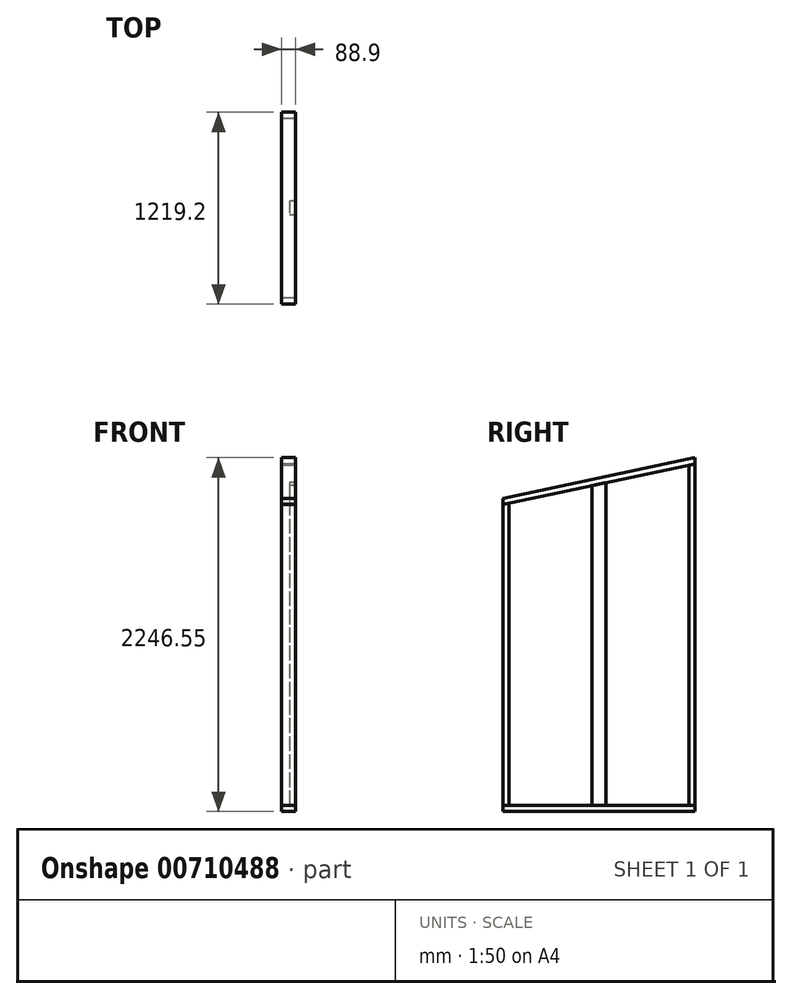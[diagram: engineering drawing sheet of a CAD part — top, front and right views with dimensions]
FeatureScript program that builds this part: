
annotation { "Feature Type Name" : "Feature", "Feature Type Description" : "" }
export const myFeature = defineFeature(function(context is Context, id is Id, definition is map)
    precondition{}
    {
        {
            var Q0;
            Q0=qCreatedBy(makeId("Right.planeOp"),FACE);
            var sketch = newSketch(context, id + "F0", { "sketchPlane" : qUnion([Q0])});
            skLineSegment(sketch, "E0", {"start": v(0, 0) * mm, "end": v(0, 1968.5) * mm});
            skLineSegment(sketch, "E1", {"start": v(0, 1968.5) * mm, "end": v(1397, 2265.44) * mm});
            skLineSegment(sketch, "E2", {"start": v(1397, 2265.44) * mm, "end": v(1397, 0) * mm});
            skLineSegment(sketch, "E3", {"start": v(1397, 0) * mm, "end": v(0, 0) * mm});
            skLineSegment(sketch, "E4", {"start": v(88.9, 0) * mm, "end": v(88.9, 1987.4) * mm});
            skLineSegment(sketch, "E5", {"start": v(1308.1, 0) * mm, "end": v(1308.1, 2246.55) * mm});
            skCircle(sketch, "E6", {"center": v(876.3, 1753.54) * mm, "radius": 381 * mm});
            skLineSegment(sketch, "E7", {"start": v(876.3, 2134.54) * mm, "end": v(876.3, 1372.54) * mm});
            skSolve(sketch);
        }
        {
            var Q0;
            Q0=qCreatedBy(makeId("Top.planeOp"),FACE);
            var sketch = newSketch(context, id + "F1", { "sketchPlane" : qUnion([Q0])});
            skLineSegment(sketch, "E8.bottom", {"start": v(0, 1308.1) * mm, "end": v(88.9, 1308.1) * mm});
            skLineSegment(sketch, "E8.top", {"start": v(0, 88.9) * mm, "end": v(88.9, 88.9) * mm});
            skLineSegment(sketch, "E8.left", {"start": v(0, 1308.1) * mm, "end": v(0, 88.9) * mm});
            skLineSegment(sketch, "E8.right", {"start": v(88.9, 1308.1) * mm, "end": v(88.9, 88.9) * mm});
            skSolve(sketch);
        }
        {
            var Q0;
            Q0=qSketchRegion(id+"F1",true);
            extrude(context, id + "F2", {"entities" : qUnion([Q0]), "depth" : 38.1 * mm, "offsetDistance" : 25.4 * mm});
        }
        {
            var Q0;
            Q0=makeQuery(id+"F2.opExtrude","CAP_FACE",FACE,{"disambiguationData":[OSD([sQuery(id+"F1.wireOp",EDGE,"E8.bottom"),sQuery(id+"F1.wireOp",EDGE,"E8.top"),sQuery(id+"F1.wireOp",EDGE,"E8.left"),sQuery(id+"F1.wireOp",EDGE,"E8.right")])],"isStart":false});
            var sketch = newSketch(context, id + "F3", { "sketchPlane" : qUnion([Q0])});
            skLineSegment(sketch, "E9.bottom", {"start": v(88.9, 127) * mm, "end": v(0, 127) * mm});
            skLineSegment(sketch, "E9.top", {"start": v(88.9, 88.9) * mm, "end": v(0, 88.9) * mm});
            skLineSegment(sketch, "E9.left", {"start": v(88.9, 127) * mm, "end": v(88.9, 88.9) * mm});
            skLineSegment(sketch, "E9.right", {"start": v(0, 127) * mm, "end": v(0, 88.9) * mm});
            skLineSegment(sketch, "E10.bottom", {"start": v(0, 1308.1) * mm, "end": v(88.9, 1308.1) * mm});
            skLineSegment(sketch, "E10.top", {"start": v(0, 1270) * mm, "end": v(88.9, 1270) * mm});
            skLineSegment(sketch, "E10.left", {"start": v(0, 1308.1) * mm, "end": v(0, 1270) * mm});
            skLineSegment(sketch, "E10.right", {"start": v(88.9, 1308.1) * mm, "end": v(88.9, 1270) * mm});
            skLineSegment(sketch, "E11", {"start": v(0, 698.5) * mm, "end": v(88.9, 698.5) * mm, "construction": true});
            skLineSegment(sketch, "E12.bottom", {"start": v(88.9, 742.95) * mm, "end": v(50.8, 742.95) * mm});
            skLineSegment(sketch, "E12.top", {"start": v(88.9, 654.05) * mm, "end": v(50.8, 654.05) * mm});
            skLineSegment(sketch, "E12.left", {"start": v(88.9, 742.95) * mm, "end": v(88.9, 654.05) * mm});
            skLineSegment(sketch, "E12.right", {"start": v(50.8, 742.95) * mm, "end": v(50.8, 654.05) * mm});
            skSolve(sketch);
        }
        {
            var Q0;
            Q0=qSketchRegion(id+"F3",true);
            extrude(context, id + "F4", {"entities" : qUnion([Q0]), "depth" : 2540 * mm, "offsetDistance" : 25.4 * mm});
        }
        {
            var Q0;
            Q0=qCreatedBy(makeId("Right.planeOp"),FACE);
            var sketch = newSketch(context, id + "F5", { "sketchPlane" : qUnion([Q0])});
            skLineSegment(sketch, "E13", {"start": v(88.9, 2578.1) * mm, "end": v(88.9, 1948.45) * mm});
            skLineSegment(sketch, "E14", {"start": v(88.9, 1948.45) * mm, "end": v(1308.1, 2207.6) * mm});
            skLineSegment(sketch, "E15", {"start": v(1308.1, 2207.6) * mm, "end": v(1308.1, 2578.1) * mm});
            skLineSegment(sketch, "E16", {"start": v(1308.1, 2578.1) * mm, "end": v(88.9, 2578.1) * mm});
            skSolve(sketch);
        }
        {
            var Q0;
            Q0=qSketchRegion(id+"F5",true);
            extrude(context, id + "F6", {"entities" : qUnion([Q0]), "operationType" : NewBodyOperationType.REMOVE, "endBound" : BoundingType.THROUGH_ALL, "depth" : 25.4 * mm, "offsetDistance" : 25.4 * mm});
        }
        {
            var Q0;
            Q0=qCreatedBy(makeId("Right.planeOp"),FACE);
            var sketch = newSketch(context, id + "F7", { "sketchPlane" : qUnion([Q0])});
            skLineSegment(sketch, "E17", {"start": v(88.9, 1948.45) * mm, "end": v(1308.1, 2207.6) * mm});
            skLineSegment(sketch, "E18", {"start": v(1308.1, 2207.6) * mm, "end": v(1308.1, 2246.55) * mm});
            skLineSegment(sketch, "E19", {"start": v(1308.1, 2246.55) * mm, "end": v(88.9, 1987.4) * mm});
            skLineSegment(sketch, "E20", {"start": v(88.9, 1987.4) * mm, "end": v(88.9, 1948.45) * mm});
            skSolve(sketch);
        }
        {
            var Q0;
            Q0=qSketchRegion(id+"F7",true);
            extrude(context, id + "F8", {"entities" : qUnion([Q0]), "depth" : 88.9 * mm, "offsetDistance" : 25.4 * mm});
        }
    });
